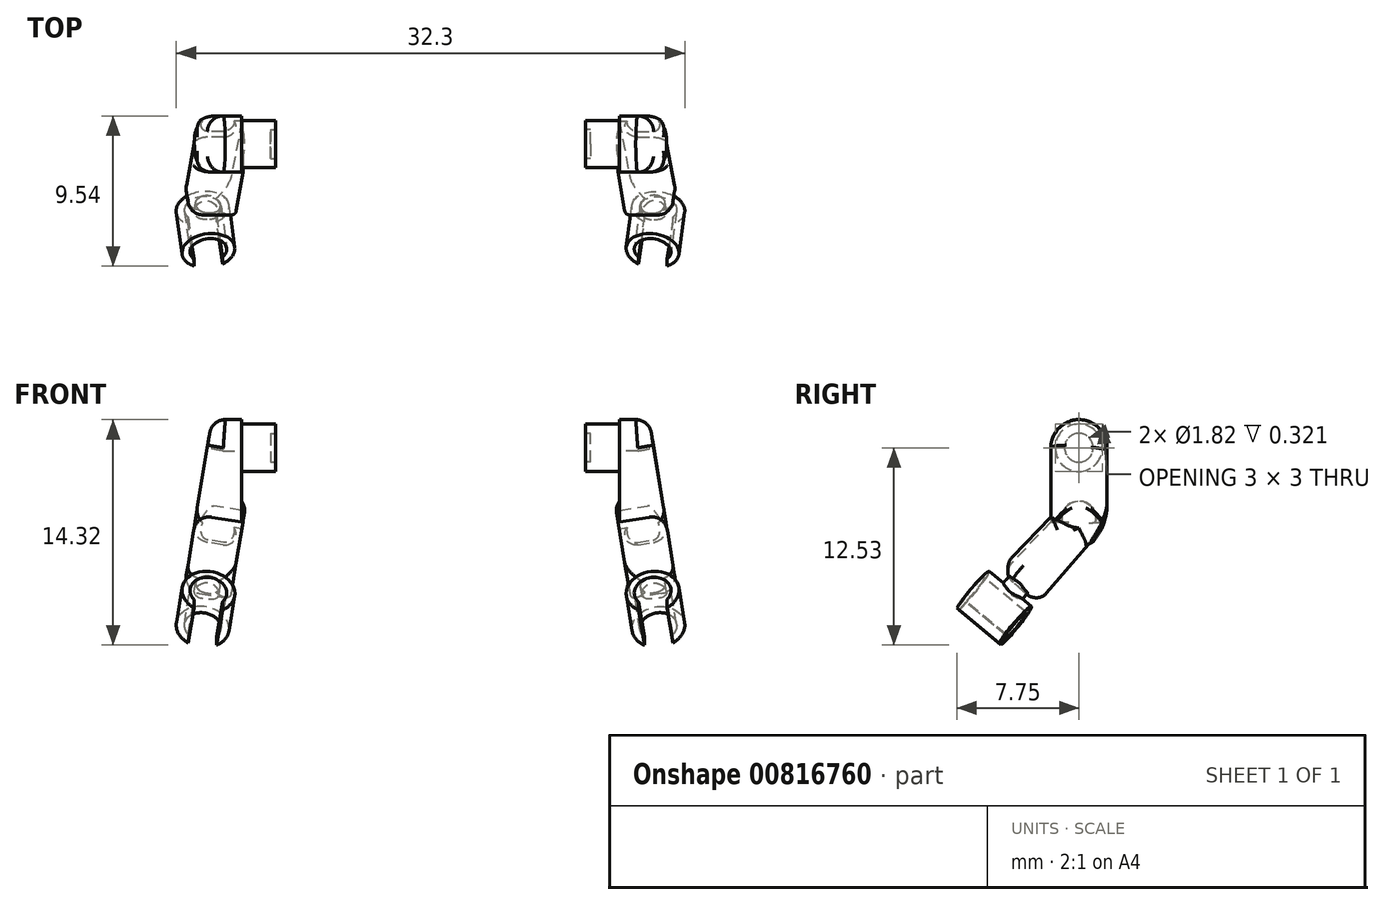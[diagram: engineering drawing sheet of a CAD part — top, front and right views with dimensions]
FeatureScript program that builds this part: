
annotation { "Feature Type Name" : "Feature", "Feature Type Description" : "" }
export const myFeature = defineFeature(function(context is Context, id is Id, definition is map)
    precondition{}
    {
        {
            var Q0;
            Q0=qCreatedBy(makeId("Right.planeOp"),FACE);
            var sketch = newSketch(context, id + "F0", { "sketchPlane" : qUnion([Q0])});
            skCircle(sketch, "E0", {"center": v(0, 0) * mm, "radius": 1.5 * mm});
            skSolve(sketch);
        }
        {
            var Q0;
            Q0 = qSketchRegion(id + "F0", true);
            extrude(context, id + "F1", {"entities" : qUnion([Q0]), "depth" : 12 * mm, "offsetDistance" : 25 * mm, "hasSecondDirection" : true, "secondDirectionOppositeDirection" : true, "secondDirectionDepth" : 12 * mm});
        }
        {
            var Q0;
            Q0=qCreatedBy(makeId("Front.planeOp"),FACE);
            var sketch = newSketch(context, id + "F2", { "sketchPlane" : qUnion([Q0])});
            skLineSegment(sketch, "E1", {"start": v(-10.16, 0) * mm, "end": v(9.84, 0) * mm});
            skLineSegment(sketch, "E2.bottom", {"start": v(-10.16, 5.47) * mm, "end": v(9.84, 5.47) * mm});
            skLineSegment(sketch, "E2.top", {"start": v(-10.16, -4.95) * mm, "end": v(9.84, -4.95) * mm});
            skLineSegment(sketch, "E2.left", {"start": v(-10.16, 5.47) * mm, "end": v(-10.16, -4.95) * mm});
            skLineSegment(sketch, "E2.right", {"start": v(9.84, 5.47) * mm, "end": v(9.84, -4.95) * mm});
            skSolve(sketch);
        }
        {
            var Q0;
            Q0 = qSketchRegion(id + "F2", true);
            extrude(context, id + "F3", {"entities" : qUnion([Q0]), "operationType" : NewBodyOperationType.REMOVE, "oppositeDirection" : true, "depth" : 25 * mm, "offsetDistance" : 25 * mm, "hasSecondDirection" : true, "secondDirectionOppositeDirection" : false, "secondDirectionDepth" : 25 * mm});
        }
        {
            var Q0;
            Q0=makeQuery(id+"F1.opExtrude","CAP_FACE",FACE,{"disambiguationData":[OSD([sQuery(id+"F0.wireOp",EDGE,"E0")])],"isStart":false});
            var sketch = newSketch(context, id + "F4", { "sketchPlane" : qUnion([Q0])});
            skCircle(sketch, "E3", {"center": v(0, 0) * mm, "radius": 1.8 * mm});
            skSolve(sketch);
        }
        {
            var Q0;
            Q0 = qSketchRegion(id + "F4", true);
            extrude(context, id + "F5", {"entities" : qUnion([Q0]), "operationType" : NewBodyOperationType.ADD, "depth" : 3 * mm, "offsetDistance" : 25 * mm});
        }
        {
            var Q0;
            Q0=makeQuery(id+"F5.opExtrude","CAP_FACE",FACE,{"disambiguationData":[OSD([sQuery(id+"F4.wireOp",EDGE,"E3")])],"isStart":true});
            var sketch = newSketch(context, id + "F6", { "sketchPlane" : qUnion([Q0])});
            skLineSegment(sketch, "E4.bottom", {"start": v(1.8, 0) * mm, "end": v(-1.78, 0) * mm});
            skLineSegment(sketch, "E4.top", {"start": v(1.8, -5) * mm, "end": v(-1.78, -5) * mm});
            skLineSegment(sketch, "E4.left", {"start": v(1.8, 0) * mm, "end": v(1.8, -5) * mm});
            skLineSegment(sketch, "E4.right", {"start": v(-1.78, 0) * mm, "end": v(-1.78, -5) * mm});
            skSolve(sketch);
        }
        {
            var Q0;
            Q0 = qSketchRegion(id + "F6", true);
            extrude(context, id + "F7", {"entities" : qUnion([Q0]), "operationType" : NewBodyOperationType.ADD, "oppositeDirection" : true, "depth" : 3 * mm, "offsetDistance" : 25 * mm});
        }
        {
            var Q0;
            Q0=makeQuery(id+"F7.opExtrude","SWEPT_FACE",FACE,{"disambiguationData":[OSD([sQuery(id+"F6.wireOp",EDGE,"E4.left")])]});
            var sketch = newSketch(context, id + "F8", { "sketchPlane" : qUnion([Q0])});
            skLineSegment(sketch, "E5", {"start": v(15, -5) * mm, "end": v(13.86, 1.95) * mm});
            skLineSegment(sketch, "E6", {"start": v(13.86, 1.95) * mm, "end": v(15, 1.95) * mm});
            skLineSegment(sketch, "E7", {"start": v(15, 1.95) * mm, "end": v(15, -5) * mm});
            skSolve(sketch);
        }
        {
            var Q0;
            Q0 = qSketchRegion(id + "F8", true);
            extrude(context, id + "F9", {"entities" : qUnion([Q0]), "operationType" : NewBodyOperationType.REMOVE, "oppositeDirection" : true, "depth" : 25 * mm, "offsetDistance" : 25 * mm});
        }
        {
            var Q0;
            Q0=makeQuery(id+"F9.boolean.opBoolean","COPY",FACE,{"derivedFrom":makeQuery(id+"F9.opExtrude","SWEPT_FACE",FACE,{"disambiguationData":[OSD([sQuery(id+"F8.wireOp",EDGE,"E5")])]})});
            fillet(context, id + "F10", {"entities" : qUnion([Q0]), "radius" : 1 * mm, "tangentPropagation" : true, "allowEdgeOverflow" : false});
        }
        {
            var Q0;
            Q0=makeQuery(id+"F9.boolean.opBoolean","COPY",FACE,{"derivedFrom":makeQuery(id+"F9.opExtrude","SWEPT_FACE",FACE,{"disambiguationData":[OSD([sQuery(id+"F8.wireOp",EDGE,"E5")])]})});
            var sketch = newSketch(context, id + "F11", { "sketchPlane" : qUnion([Q0])});
            skLineSegment(sketch, "E8", {"start": v(1.77, -6.65) * mm, "end": v(-2.72, -11.95) * mm});
            skLineSegment(sketch, "E9", {"start": v(-1.78, -6.6) * mm, "end": v(-4.93, -9.92) * mm});
            skLineSegment(sketch, "E10", {"start": v(-4.93, -9.92) * mm, "end": v(-1.78, -6.6) * mm});
            skLineSegment(sketch, "E11", {"start": v(1.77, -6.65) * mm, "end": v(-1.78, -6.6) * mm});
            skLineSegment(sketch, "E12", {"start": v(-4.93, -9.92) * mm, "end": v(-2.72, -11.95) * mm});
            skSolve(sketch);
        }
        {
            var Q0;
            Q0 = qSketchRegion(id + "F11", true);
            extrude(context, id + "F12", {"entities" : qUnion([Q0]), "oppositeDirection" : true, "depth" : 3 * mm, "offsetDistance" : 25 * mm});
        }
        {
            var Q0;
            Q0=makeQuery(id+"F12.opExtrude","CAP_FACE",FACE,{"disambiguationData":[OSD([sQuery(id+"F11.wireOp",EDGE,"E8"),sQuery(id+"F11.wireOp",EDGE,"E10"),sQuery(id+"F11.wireOp",EDGE,"E11"),sQuery(id+"F11.wireOp",EDGE,"E12")])],"isStart":true});
            var Q1;
            Q1=makeQuery(id+"F12.opExtrude","SWEPT_FACE",FACE,{"disambiguationData":[OSD([sQuery(id+"F11.wireOp",EDGE,"E12")])]});
            fillet(context, id + "F13", {"entities" : qUnion([Q0, Q1]), "radius" : 1 * mm, "tangentPropagation" : true, "allowEdgeOverflow" : false});
        }
        {
            var Q0;
            Q0=makeQuery(id+"F9.boolean.opBoolean","COPY",FACE,{"derivedFrom":makeQuery(id+"F9.opExtrude","SWEPT_FACE",FACE,{"disambiguationData":[OSD([sQuery(id+"F8.wireOp",EDGE,"E5")])]})});
            var sketch = newSketch(context, id + "F14", { "sketchPlane" : qUnion([Q0])});
            skArc(sketch, "E13", {"start": v(0.24, -8.65) * mm, "mid": v(1.3, -7.36) * mm, "end": v(1.8, -5.77) * mm});
            skArc(sketch, "E14", {"start": v(0.24, -8.65) * mm, "mid": v(2.45, -7.98) * mm, "end": v(1.8, -5.77) * mm});
            skSolve(sketch);
        }
        {
            var Q0;
            Q0 = qSketchRegion(id + "F14", true);
            extrude(context, id + "F15", {"entities" : qUnion([Q0]), "operationType" : NewBodyOperationType.REMOVE, "oppositeDirection" : true, "depth" : 4 * mm, "offsetDistance" : 25 * mm});
        }
        {
            var Q0;
            Q0=makeQuery(id+"F9.boolean.opBoolean","COPY",FACE,{"derivedFrom":makeQuery(id+"F9.opExtrude","SWEPT_FACE",FACE,{"disambiguationData":[OSD([sQuery(id+"F8.wireOp",EDGE,"E5")])]})});
            var sketch = newSketch(context, id + "F16", { "sketchPlane" : qUnion([Q0])});
            skCircle(sketch, "E15", {"center": v(0, -6.65) * mm, "radius": 1.64 * mm});
            skSolve(sketch);
        }
        {
            var Q0;
            Q0 = qSketchRegion(id + "F16", true);
            extrude(context, id + "F17", {"entities" : qUnion([Q0]), "oppositeDirection" : true, "depth" : 3 * mm, "offsetDistance" : 25 * mm});
        }
        {
            var Q0;
            Q0=makeQuery(id+"F17.opExtrude","CAP_FACE",FACE,{"disambiguationData":[OSD([sQuery(id+"F16.wireOp",EDGE,"E15")])],"isStart":true});
            var Q1;
            Q1=makeQuery(id+"F17.opExtrude","CAP_FACE",FACE,{"disambiguationData":[OSD([sQuery(id+"F16.wireOp",EDGE,"E15")])],"isStart":false});
            var Q2;
            Q2=makeQuery(id+"F17.opExtrude","SWEPT_FACE",FACE,{"disambiguationData":[OSD([sQuery(id+"F16.wireOp",EDGE,"E15")])]});
            fillet(context, id + "F18", {"entities" : qUnion([Q0, Q1, Q2]), "radius" : 1 * mm, "tangentPropagation" : true, "allowEdgeOverflow" : false});
        }
        {
            var Q0;
            Q0 = qSketchRegion(id + "F14", true);
            extrude(context, id + "F19", {"entities" : qUnion([Q0]), "operationType" : NewBodyOperationType.REMOVE, "oppositeDirection" : true, "depth" : 25 * mm, "offsetDistance" : 25 * mm});
        }
        {
            var Q0;
            Q0=makeQuery(id+"F12.opExtrude","SWEPT_FACE",FACE,{"disambiguationData":[OSD([sQuery(id+"F11.wireOp",EDGE,"E12")])]});
            var sketch = newSketch(context, id + "F20", { "sketchPlane" : qUnion([Q0])});
            skCircle(sketch, "E16", {"center": v(12.96, -3.14) * mm, "radius": 0.79 * mm});
            skSolve(sketch);
        }
        {
            var Q0;
            Q0 = qSketchRegion(id + "F20", true);
            extrude(context, id + "F21", {"entities" : qUnion([Q0]), "operationType" : NewBodyOperationType.ADD, "depth" : 1 * mm, "offsetDistance" : 25 * mm, "hasSecondDirection" : true, "secondDirectionOppositeDirection" : true, "secondDirectionDepth" : 1 * mm});
        }
        {
            var Q0;
            Q0=makeQuery(id+"F12.opExtrude","SWEPT_FACE",FACE,{"disambiguationData":[OSD([sQuery(id+"F11.wireOp",EDGE,"E8")])]});
            var sketch = newSketch(context, id + "F22", { "sketchPlane" : qUnion([Q0])});
            skCircle(sketch, "E17", {"center": v(-13.96, -11.35) * mm, "radius": 1.69 * mm});
            skSolve(sketch);
        }
        {
            var Q0;
            Q0 = qSketchRegion(id + "F22", true);
            extrude(context, id + "F23", {"entities" : qUnion([Q0]), "operationType" : NewBodyOperationType.ADD, "oppositeDirection" : true, "depth" : 3.5 * mm, "offsetDistance" : 25 * mm});
        }
        {
            var Q0;
            Q0=makeQuery(id+"F23.opExtrude","CAP_FACE",FACE,{"disambiguationData":[OSD([sQuery(id+"F22.wireOp",EDGE,"E17")])],"isStart":false});
            var sketch = newSketch(context, id + "F24", { "sketchPlane" : qUnion([Q0])});
            skCircle(sketch, "E18", {"center": v(13.96, -11.35) * mm, "radius": 1.17 * mm});
            skLineSegment(sketch, "E19.bottom", {"start": v(13.06, -11.8) * mm, "end": v(14.88, -11.8) * mm});
            skLineSegment(sketch, "E19.top", {"start": v(13.06, -13.33) * mm, "end": v(14.88, -13.33) * mm});
            skLineSegment(sketch, "E19.left", {"start": v(13.06, -11.8) * mm, "end": v(13.06, -13.33) * mm});
            skLineSegment(sketch, "E19.right", {"start": v(14.88, -11.8) * mm, "end": v(14.88, -13.33) * mm});
            skSolve(sketch);
        }
        {
            var Q0;
            Q0 = qSketchRegion(id + "F24", true);
            extrude(context, id + "F25", {"entities" : qUnion([Q0]), "operationType" : NewBodyOperationType.REMOVE, "oppositeDirection" : true, "depth" : 25 * mm, "offsetDistance" : 25 * mm});
        }
        {
            var Q0;
            Q0=makeQuery(id+"F3.boolean.opBoolean","COPY",FACE,{"derivedFrom":makeQuery(id+"F3.opExtrude","SWEPT_FACE",FACE,{"disambiguationData":[OSD([sQuery(id+"F2.wireOp",EDGE,"E2.right")])]})});
            var sketch = newSketch(context, id + "F26", { "sketchPlane" : qUnion([Q0])});
            skCircle(sketch, "E20", {"center": v(0, 0) * mm, "radius": 0.9 * mm});
            skSolve(sketch);
        }
        {
            var Q0;
            Q0 = qSketchRegion(id + "F26", true);
            extrude(context, id + "F27", {"entities" : qUnion([Q0]), "operationType" : NewBodyOperationType.REMOVE, "oppositeDirection" : true, "depth" : 1 * mm, "offsetDistance" : 25 * mm});
        }
        {
            var Q0;
            Q0=makeQuery(id+"F3.boolean.opBoolean","SPLIT",BODY,{"disambiguationData":[OD(1.0)],"derivedFrom":makeQuery(id+"F1.opExtrude","SWEPT_BODY",BODY,{"disambiguationData":[OSD([sQuery(id+"F0.wireOp",EDGE,"E0")])]})});
            var Q1;
            Q1=makeQuery(id+"F17.opExtrude","SWEPT_BODY",BODY,{"disambiguationData":[OSD([sQuery(id+"F16.wireOp",EDGE,"E15")])]});
            var Q2;
            Q2=makeQuery(id+"F23.opExtrude","SWEPT_BODY",BODY,{"disambiguationData":[OSD([sQuery(id+"F22.wireOp",EDGE,"E17")])]});
            var Q3;
            Q3=makeQuery(id+"F12.opExtrude","SWEPT_BODY",BODY,{"disambiguationData":[OSD([sQuery(id+"F11.wireOp",EDGE,"E8"),sQuery(id+"F11.wireOp",EDGE,"E10"),sQuery(id+"F11.wireOp",EDGE,"E11"),sQuery(id+"F11.wireOp",EDGE,"E12")])]});
            var Q4;
            Q4=qCreatedBy(makeId("Right.planeOp"),FACE);
            mirror(context, id + "F28", {"operationType" : NewBodyOperationType.ADD, "entities" : qUnion([Q0, Q1, Q2, Q3]), "mirrorPlane" : qUnion([Q4])});
        }
    });
